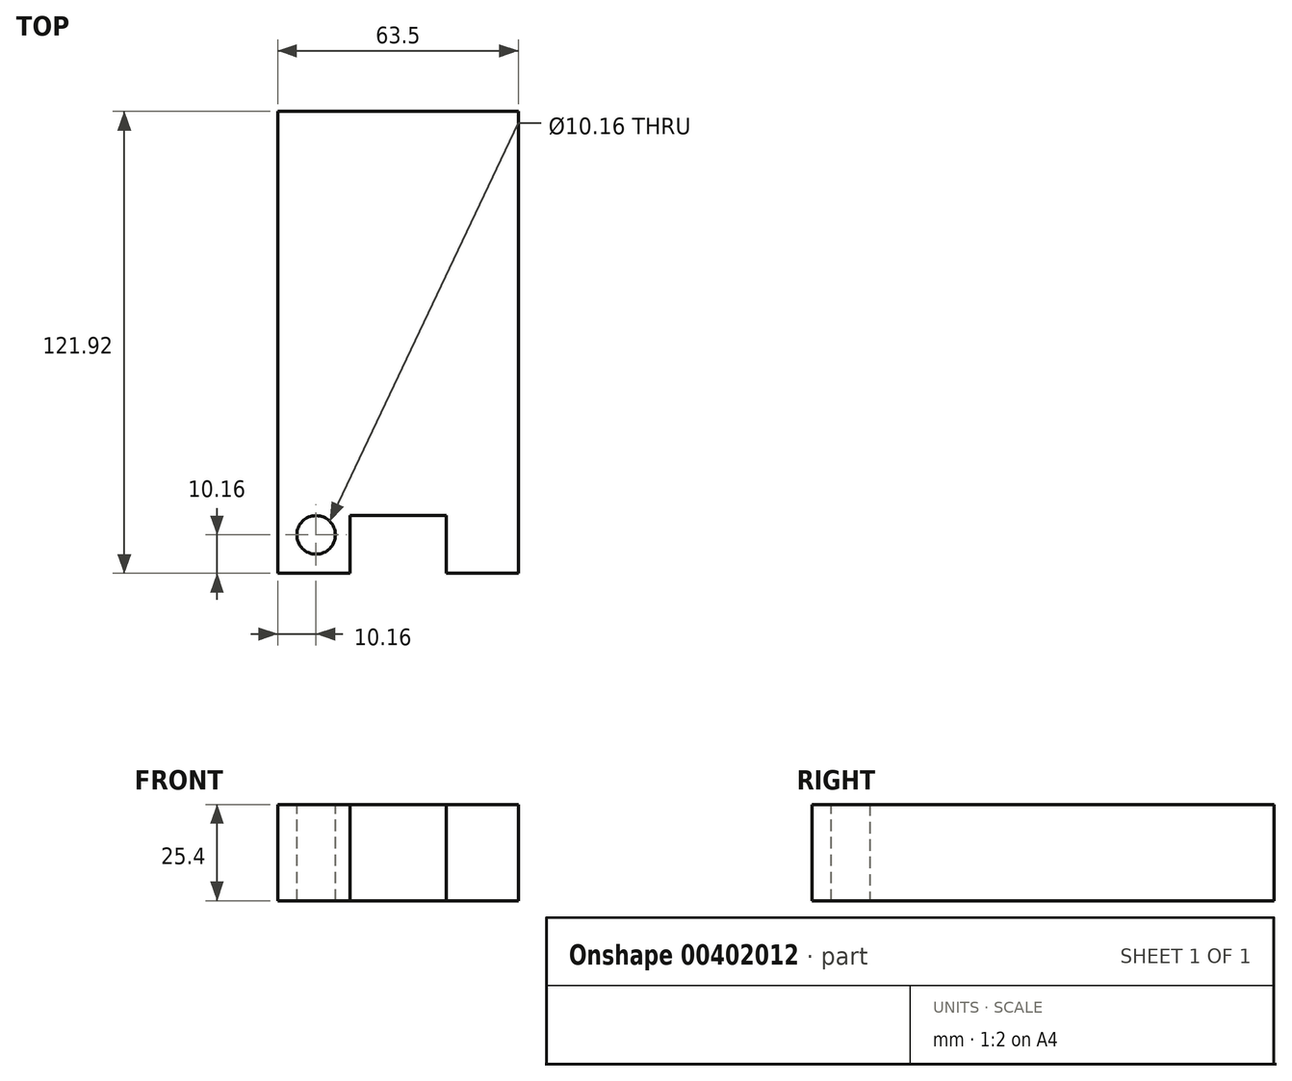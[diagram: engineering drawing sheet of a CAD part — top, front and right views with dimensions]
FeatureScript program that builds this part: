
annotation { "Feature Type Name" : "Feature", "Feature Type Description" : "" }
export const myFeature = defineFeature(function(context is Context, id is Id, definition is map)
    precondition{}
    {
        {
            var Q0;
            Q0=qCreatedBy(makeId("Top.planeOp"),FACE);
            var sketch = newSketch(context, id + "F0", { "sketchPlane" : qUnion([Q0])});
            skLineSegment(sketch, "E0.bottom", {"start": v(31.75, 60.96) * mm, "end": v(-31.75, 60.96) * mm});
            skLineSegment(sketch, "E0.left", {"start": v(31.75, 60.96) * mm, "end": v(31.75, -60.96) * mm});
            skLineSegment(sketch, "E0.right", {"start": v(-31.75, 60.96) * mm, "end": v(-31.75, -60.96) * mm});
            skPoint(sketch, "E0.middle", {"position": v(0, 0) * mm});
            skLineSegment(sketch, "E1.top", {"start": v(-12.7, -45.72) * mm, "end": v(12.7, -45.72) * mm});
            skLineSegment(sketch, "E1.left", {"start": v(-12.7, -60.96) * mm, "end": v(-12.7, -45.72) * mm});
            skLineSegment(sketch, "E1.right", {"start": v(12.7, -60.96) * mm, "end": v(12.7, -45.72) * mm});
            skLineSegment(sketch, "E2", {"start": v(-31.75, -60.96) * mm, "end": v(-12.7, -60.96) * mm});
            skLineSegment(sketch, "E3", {"start": v(12.7, -60.96) * mm, "end": v(31.75, -60.96) * mm});
            skSolve(sketch);
        }
        {
            var Q0;
            Q0 = qSketchRegion(id + "F0", true);
            extrude(context, id + "F1", {"entities" : qUnion([Q0]), "depth" : 25.4 * mm});
        }
        {
            var Q0;
            Q0=makeQuery(id+"F1.opExtrude","CAP_FACE",FACE,{"disambiguationData":[OSD([sQuery(id+"F0.wireOp",EDGE,"E0.bottom"),sQuery(id+"F0.wireOp",EDGE,"E0.left"),sQuery(id+"F0.wireOp",EDGE,"E0.right"),sQuery(id+"F0.wireOp",EDGE,"E1.top"),sQuery(id+"F0.wireOp",EDGE,"E1.left"),sQuery(id+"F0.wireOp",EDGE,"E1.right"),sQuery(id+"F0.wireOp",EDGE,"E2"),sQuery(id+"F0.wireOp",EDGE,"E3")])],"isStart":false});
            var sketch = newSketch(context, id + "F2", { "sketchPlane" : qUnion([Q0])});
            skCircle(sketch, "E4", {"center": v(-21.59, -50.8) * mm, "radius": 5.08 * mm});
            skSolve(sketch);
        }
        {
            var Q0;
            Q0 = qSketchRegion(id + "F2", true);
            extrude(context, id + "F3", {"entities" : qUnion([Q0]), "operationType" : NewBodyOperationType.REMOVE, "oppositeDirection" : true, "depth" : 25.4 * mm});
        }
    });
